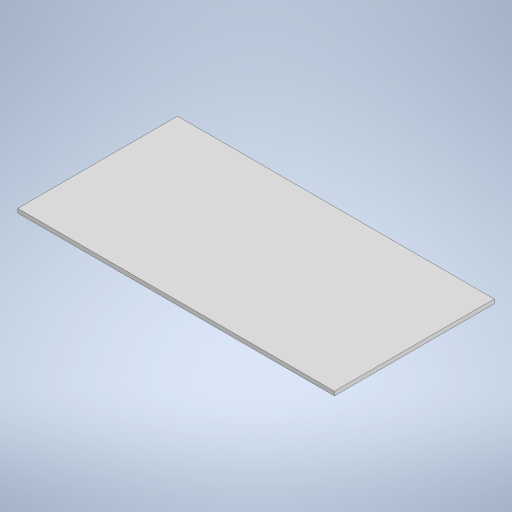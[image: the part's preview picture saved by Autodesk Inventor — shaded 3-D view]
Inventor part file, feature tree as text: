
AUTODESK INVENTOR PART (.ipt)
format: ipt  version: 2023 (Build 270158000, 158)  size: 208,384 bytes
history: native  units: in
note: dims shown in document units (in); Inventor stores cm internally (conversion verified against a paired STEP export)
features: extrude x1, sketch x1
ambient origin geometry x8: Origin, YZ Plane, XZ Plane, XY Plane, X Axis, Y Axis, Z Axis, Center Point
bodies: Solid1 (feature_tree)
feature tree (2):
  extrude  "Extrusion1"  Depth=15.3858in
  sketch  "Sketch1"  dims[d0=30.5039in d1=15.3858in d2=0.3937in d3=0.0in]
